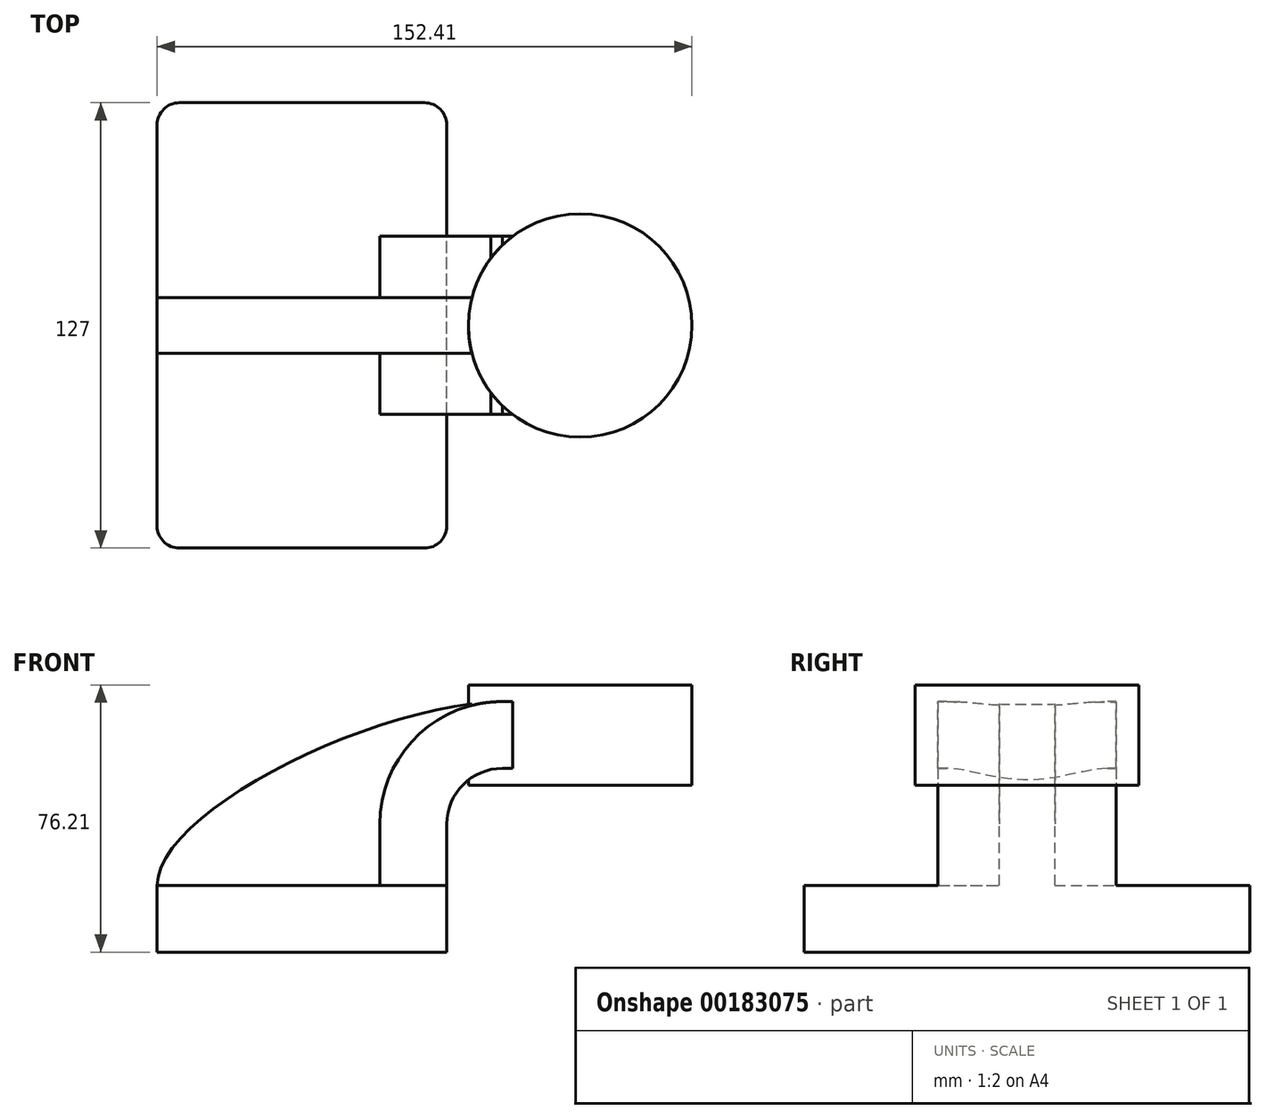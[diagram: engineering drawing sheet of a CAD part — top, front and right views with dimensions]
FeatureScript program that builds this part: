
annotation { "Feature Type Name" : "Feature", "Feature Type Description" : "" }
export const myFeature = defineFeature(function(context is Context, id is Id, definition is map)
    precondition{}
    {
        {
            var Q0;
            Q0=qCreatedBy(makeId("Front.planeOp"),FACE);
            var sketch = newSketch(context, id + "F0", { "sketchPlane" : qUnion([Q0])});
            skLineSegment(sketch, "E0.bottom", {"start": v(-41.28, 9.52) * mm, "end": v(41.27, 9.53) * mm});
            skLineSegment(sketch, "E0.top", {"start": v(-41.28, -9.53) * mm, "end": v(41.28, -9.53) * mm});
            skLineSegment(sketch, "E0.left", {"start": v(-41.28, 9.52) * mm, "end": v(-41.27, -9.53) * mm});
            skLineSegment(sketch, "E0.right", {"start": v(41.28, 9.53) * mm, "end": v(41.28, -9.52) * mm});
            skPoint(sketch, "E0.middle", {"position": v(0, 0) * mm});
            skLineSegment(sketch, "E1.bottom", {"start": v(60.33, 38.1) * mm, "end": v(111.13, 38.1) * mm});
            skLineSegment(sketch, "E1.top", {"start": v(60.33, 66.67) * mm, "end": v(111.13, 66.67) * mm});
            skLineSegment(sketch, "E1.left", {"start": v(60.33, 38.1) * mm, "end": v(60.33, 66.67) * mm});
            skLineSegment(sketch, "E1.right", {"start": v(111.13, 38.1) * mm, "end": v(111.13, 66.67) * mm});
            skPoint(sketch, "E1.middle", {"position": v(85.73, 52.39) * mm});
            skLineSegment(sketch, "E2", {"start": v(41.27, 9.53) * mm, "end": v(41.27, 27) * mm});
            skArc(sketch, "E3", {"start": v(41.27, 27) * mm, "mid": v(45.92, 38.23) * mm, "end": v(57.15, 42.88) * mm});
            skLineSegment(sketch, "E4", {"start": v(57.15, 42.88) * mm, "end": v(79.27, 42.88) * mm});
            skLineSegment(sketch, "E5.0", {"start": v(57.15, 61.93) * mm, "end": v(79.27, 61.93) * mm});
            skArc(sketch, "E5.1", {"start": v(22.22, 27) * mm, "mid": v(32.45, 51.7) * mm, "end": v(57.15, 61.93) * mm});
            skLineSegment(sketch, "E5.2", {"start": v(22.22, 9.53) * mm, "end": v(22.22, 27) * mm});
            skFitSpline(sketch, "E6", {"points": [v(-41.28, 9.53) * mm, v(57.15, 61.93) * mm], "startDerivative": vector(0.02, 61.78) * mm, "endDerivative": vector(115.33, 3.14) * mm});
            skLineSegment(sketch, "E7", {"start": v(79.27, 66.67) * mm, "end": v(79.27, 38.1) * mm});
            skLineSegment(sketch, "E8", {"start": v(79.27, 38.1) * mm, "end": v(79.27, 49.5) * mm});
            skSolve(sketch);
        }
        {
            var Q0;
            Q0=makeQuery(id+"F0.imprint","IMPRINT",FACE,{"disambiguationData":[TD([[makeQuery(id+"F0.imprint","IMPRINT",EDGE,{"derivedFrom":sQuery(id+"F0.wireOp",EDGE,"E0.top")}),1.0]])]});
            extrude(context, id + "F1", {"entities" : qUnion([Q0]), "endBound" : BoundingType.SYMMETRIC, "depth" : 127 * mm});
        }
        {
            var Q0;
            {var subQ1=sQuery(id+"F0.wireOp",EDGE,"E2");Q0=makeQuery(id+"F0.imprint","IMPRINT",FACE,{"disambiguationData":[TD([[makeQuery(id+"F0.imprint","IMPRINT",EDGE,{"derivedFrom":subQ1}),1.0]])]});}
            var Q1;
            {var subQ3=sQuery(id+"F0.wireOp",EDGE,"E1.left");var subQ7=sQuery(id+"F0.wireOp",EDGE,"E4");var subQ9=makeQuery(id+"F0.imprint","INTERSECT",VERTEX,{"derivedFrom":[subQ3,subQ7]});Q1=makeQuery(id+"F0.imprint","IMPRINT",FACE,{"disambiguationData":[TD([[makeQuery(id+"F0.imprint","IMPRINT",EDGE,{"disambiguationData":[TD([[subQ9,-1.0]])],"derivedFrom":subQ3}),-1.0]])]});}
            extrude(context, id + "F2", {"entities" : qUnion([Q0, Q1]), "operationType" : NewBodyOperationType.ADD, "endBound" : BoundingType.SYMMETRIC, "depth" : 50.8 * mm});
        }
        {
            var Q0;
            {var subQ3=sQuery(id+"F0.wireOp",EDGE,"E5.2");Q0=makeQuery(id+"F0.imprint","IMPRINT",FACE,{"disambiguationData":[TD([[makeQuery(id+"F0.imprint","IMPRINT",EDGE,{"derivedFrom":subQ3}),1.0]])]});}
            extrude(context, id + "F3", {"entities" : qUnion([Q0]), "operationType" : NewBodyOperationType.ADD, "endBound" : BoundingType.SYMMETRIC, "depth" : 15.88 * mm});
        }
        {
            var Q0;
            {var subQ0=sQuery(id+"F0.wireOp",EDGE,"E1.right");Q0=makeQuery(id+"F0.imprint","IMPRINT",FACE,{"disambiguationData":[TD([[makeQuery(id+"F0.imprint","IMPRINT",EDGE,{"derivedFrom":subQ0}),1.0]])]});}
            var Q1;
            Q1=sQuery(id+"F0.wireOp",EDGE,"E7");
            revolve(context, id + "F4", {"operationType" : NewBodyOperationType.ADD, "entities" : qUnion([Q0]), "axis" : qUnion([Q1]), "revolveType" : RevolveType.FULL});
        }
        {
            var Q0;
            Q0=makeQuery(id+"F1.opExtrude","CAP_EDGE",EDGE,{"disambiguationData":[OSD([sQuery(id+"F0.wireOp",EDGE,"E0.right")])],"isStart":false});
            var Q1;
            Q1=makeQuery(id+"F1.opExtrude","CAP_EDGE",EDGE,{"disambiguationData":[OSD([sQuery(id+"F0.wireOp",EDGE,"E0.left")])],"isStart":false});
            var Q2;
            Q2=makeQuery(id+"F1.opExtrude","CAP_EDGE",EDGE,{"disambiguationData":[OSD([sQuery(id+"F0.wireOp",EDGE,"E0.right")])],"isStart":true});
            var Q3;
            Q3=makeQuery(id+"F1.opExtrude","CAP_EDGE",EDGE,{"disambiguationData":[OSD([sQuery(id+"F0.wireOp",EDGE,"E0.left")])],"isStart":true});
            fillet(context, id + "F5", {"entities" : qUnion([Q0, Q1, Q2, Q3]), "radius" : 6.35 * mm, "tangentPropagation" : true, "allowEdgeOverflow" : false});
        }
    });
